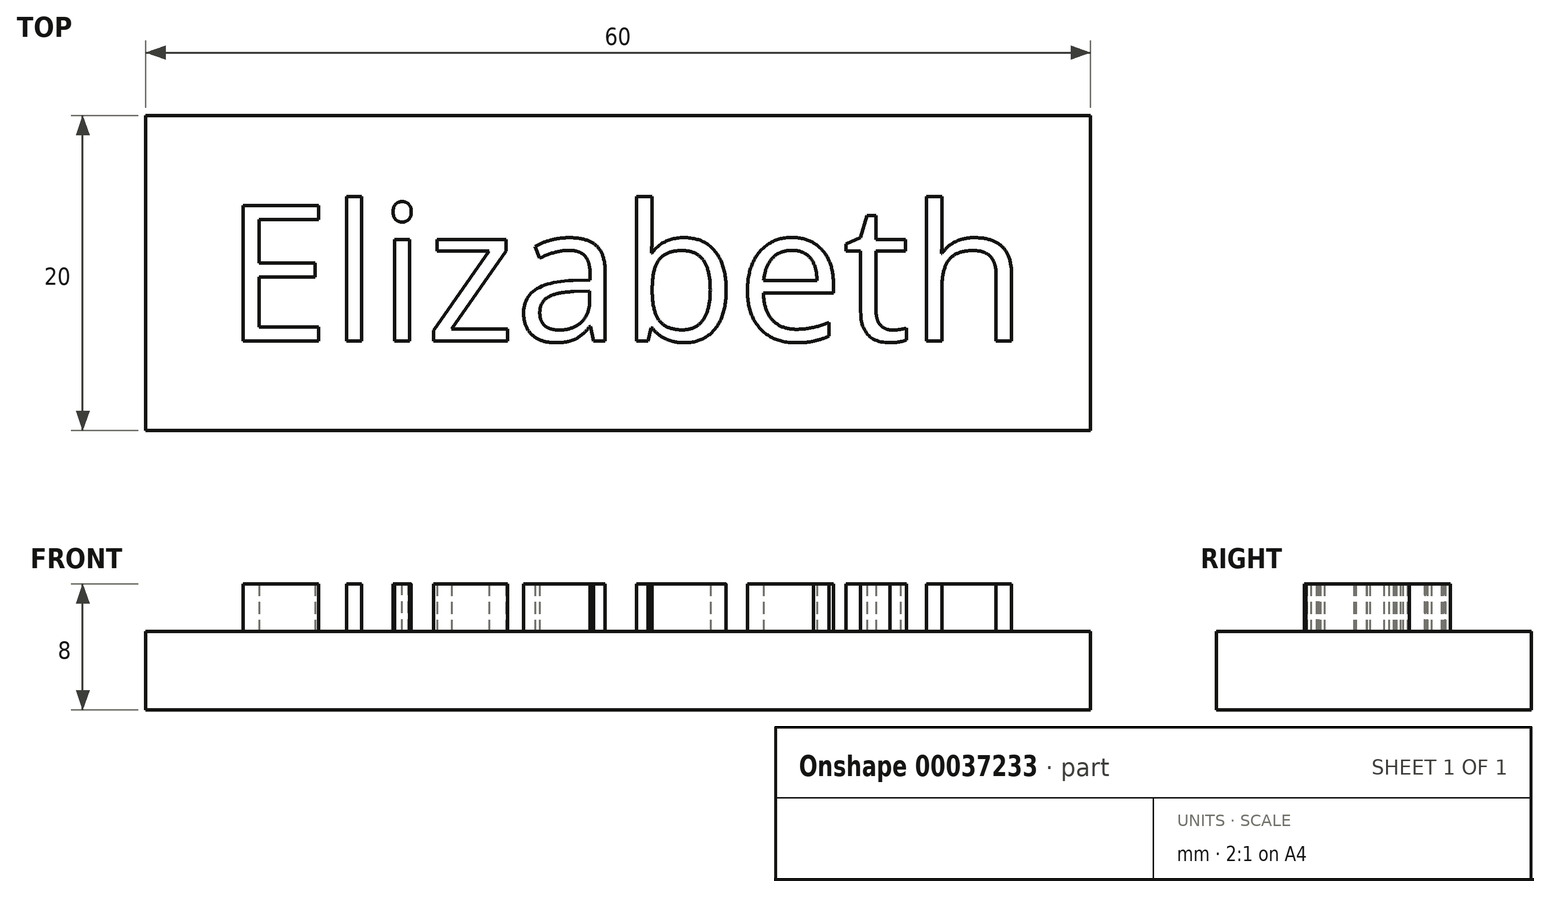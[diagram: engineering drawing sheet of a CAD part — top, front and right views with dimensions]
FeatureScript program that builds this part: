
annotation { "Feature Type Name" : "Feature", "Feature Type Description" : "" }
export const myFeature = defineFeature(function(context is Context, id is Id, definition is map)
    precondition{}
    {
        {
            var Q0;
            Q0=qCreatedBy(makeId("Top.planeOp"),FACE);
            var sketch = newSketch(context, id + "F0", { "sketchPlane" : qUnion([Q0])});
            skLineSegment(sketch, "E0.rect.bottom", {"start": v(-30, 10) * mm, "end": v(30, 10) * mm});
            skLineSegment(sketch, "E0.rect.top", {"start": v(-30, -10) * mm, "end": v(30, -10) * mm});
            skLineSegment(sketch, "E0.rect.left", {"start": v(-30, 10) * mm, "end": v(-30, -10) * mm});
            skLineSegment(sketch, "E0.rect.right", {"start": v(30, 10) * mm, "end": v(30, -10) * mm});
            skPoint(sketch, "E0.rect.middle", {"position": v(0, 0) * mm});
            skSolve(sketch);
        }
        {
            var Q0;
            Q0 = qSketchRegion(id + "F0", true);
            extrude(context, id + "F1", {"entities" : qUnion([Q0]), "depth" : 5 * mm});
        }
        {
            var Q0;
            Q0=makeQuery(id+"F1.opExtrude","CAP_FACE",FACE,{"disambiguationData":[OSD([sQuery(id+"F0.wireOp",EDGE,"E0.rect.bottom"),sQuery(id+"F0.wireOp",EDGE,"E0.rect.top"),sQuery(id+"F0.wireOp",EDGE,"E0.rect.left"),sQuery(id+"F0.wireOp",EDGE,"E0.rect.right")])],"isStart":false});
            var sketch = newSketch(context, id + "F2", { "sketchPlane" : qUnion([Q0])});
            skText(sketch, "E1", { "text": "Elizabeth", "fontName": "OpenSans-Regular.ttf"});
            const initialGuessF2  = {"E1": [-0.025, -0.00431, 1, 0, 0.00868]};
            skSetInitialGuess(sketch, initialGuessF2);
            skSolve(sketch);
        }
        {
            var Q0;
            Q0 = qSketchRegion(id + "F2", true);
            extrude(context, id + "F3", {"entities" : qUnion([Q0]), "operationType" : NewBodyOperationType.ADD, "depth" : 3 * mm});
        }
    });
